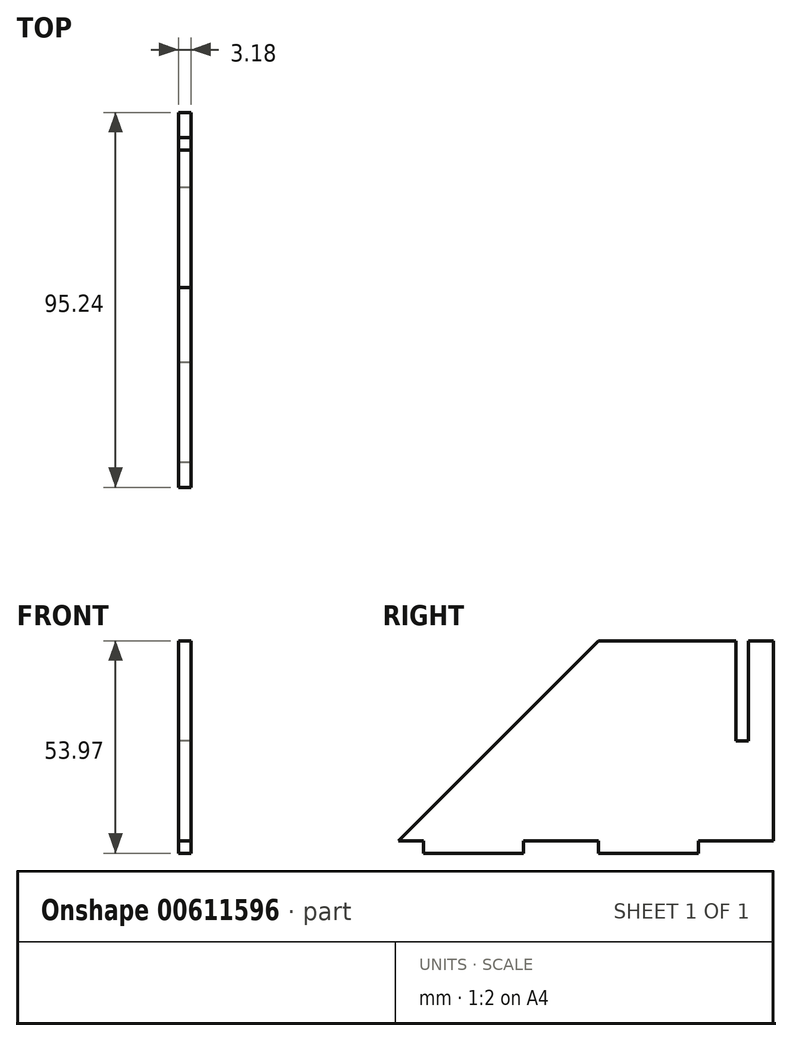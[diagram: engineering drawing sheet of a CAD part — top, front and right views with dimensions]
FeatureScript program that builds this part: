
annotation { "Feature Type Name" : "Feature", "Feature Type Description" : "" }
export const myFeature = defineFeature(function(context is Context, id is Id, definition is map)
    precondition{}
    {
        {
            var Q0;
            Q0=qCreatedBy(makeId("Right.planeOp"),FACE);
            var sketch = newSketch(context, id + "F0", { "sketchPlane" : qUnion([Q0])});
            skLineSegment(sketch, "E0", {"start": v(47.63, -25.4) * mm, "end": v(47.62, 25.4) * mm});
            skLineSegment(sketch, "E1", {"start": v(47.62, 25.4) * mm, "end": v(41.27, 25.4) * mm});
            skLineSegment(sketch, "E2", {"start": v(3.18, 25.4) * mm, "end": v(-47.63, -25.4) * mm});
            skLineSegment(sketch, "E3", {"start": v(-47.63, -25.4) * mm, "end": v(-41.28, -25.4) * mm});
            skLineSegment(sketch, "E4", {"start": v(-41.28, -25.4) * mm, "end": v(-41.28, -28.58) * mm});
            skLineSegment(sketch, "E5", {"start": v(-41.28, -28.58) * mm, "end": v(-15.88, -28.58) * mm});
            skLineSegment(sketch, "E6", {"start": v(-15.88, -28.58) * mm, "end": v(-15.88, -25.4) * mm});
            skLineSegment(sketch, "E7", {"start": v(3.17, -25.4) * mm, "end": v(3.17, -28.58) * mm});
            skLineSegment(sketch, "E8", {"start": v(3.17, -28.58) * mm, "end": v(28.57, -28.58) * mm});
            skLineSegment(sketch, "E9", {"start": v(28.57, -28.58) * mm, "end": v(28.57, -25.4) * mm});
            skLineSegment(sketch, "E10.trimOffspring", {"start": v(28.57, -25.4) * mm, "end": v(47.63, -25.4) * mm});
            skLineSegment(sketch, "E11.trimOffspring", {"start": v(-15.88, -25.4) * mm, "end": v(3.17, -25.4) * mm});
            skLineSegment(sketch, "E12", {"start": v(41.27, 25.4) * mm, "end": v(41.28, 0) * mm});
            skLineSegment(sketch, "E13", {"start": v(41.28, 0) * mm, "end": v(38.1, 0) * mm});
            skLineSegment(sketch, "E14", {"start": v(38.1, 0) * mm, "end": v(38.1, 25.4) * mm});
            skLineSegment(sketch, "E15.trimOffspring", {"start": v(38.1, 25.4) * mm, "end": v(3.17, 25.4) * mm});
            skSolve(sketch);
        }
        {
            var Q0;
            Q0 = qSketchRegion(id + "F0", true);
            extrude(context, id + "F1", {"entities" : qUnion([Q0]), "endBound" : BoundingType.SYMMETRIC, "depth" : 3.17 * mm, "offsetDistance" : 25.4 * mm});
        }
    });
